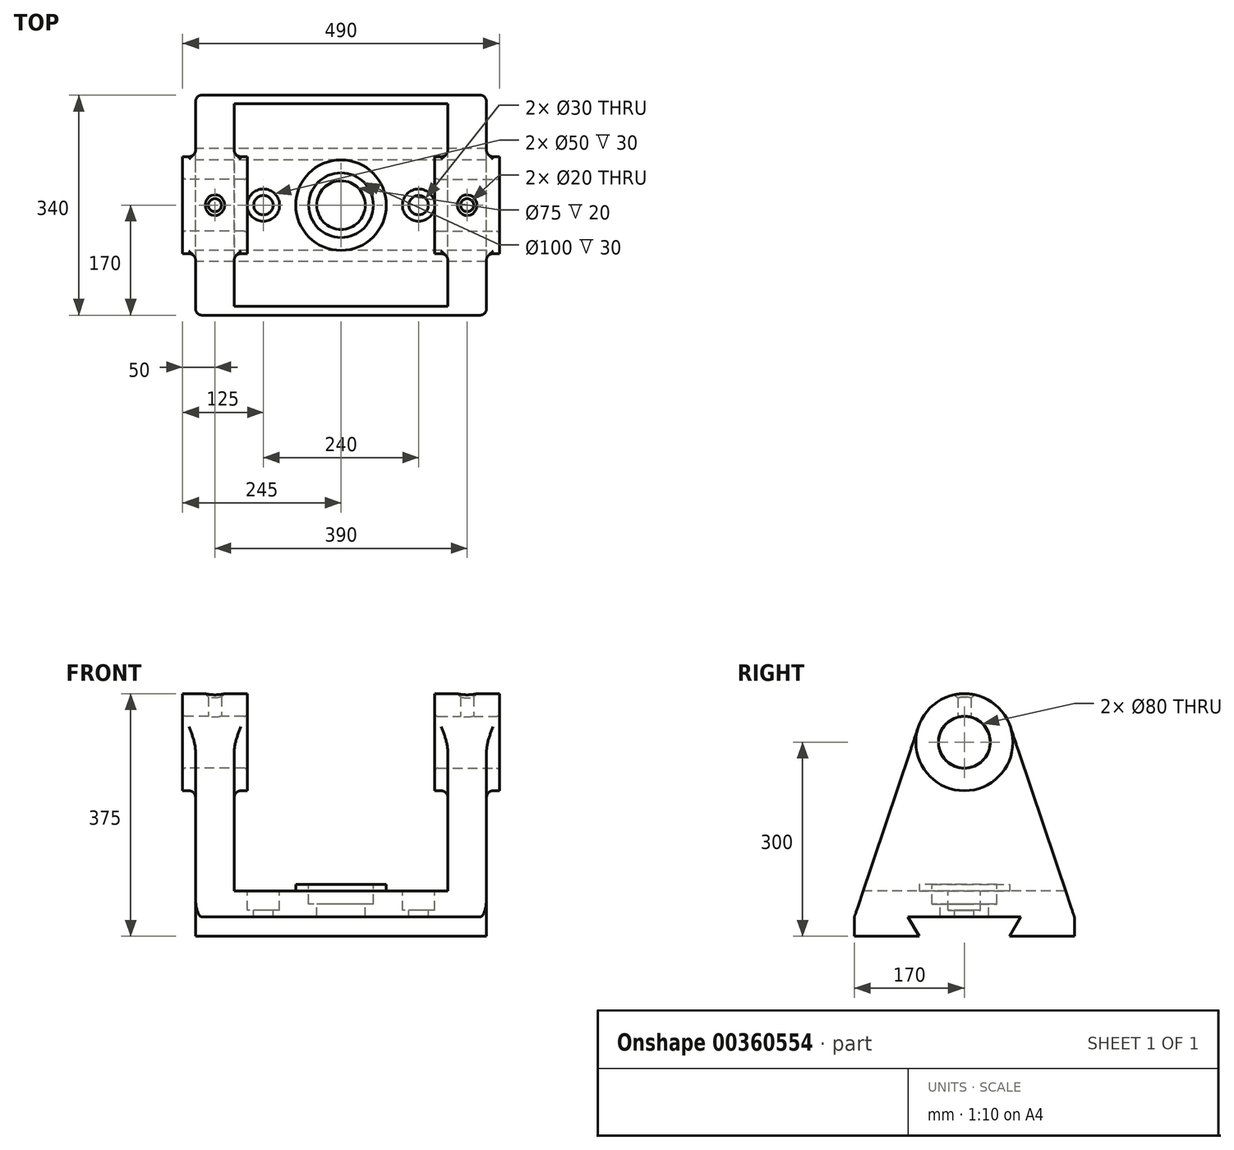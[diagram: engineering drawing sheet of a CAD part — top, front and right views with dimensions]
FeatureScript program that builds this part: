
annotation { "Feature Type Name" : "Feature", "Feature Type Description" : "" }
export const myFeature = defineFeature(function(context is Context, id is Id, definition is map)
    precondition{}
    {
        {
            var Q0;
            Q0=qCreatedBy(makeId("Right.planeOp"),FACE);
            var sketch = newSketch(context, id + "F0", { "sketchPlane" : qUnion([Q0])});
            skArc(sketch, "E0", {"start": v(71.08, 23.92) * mm, "mid": v(0, 75) * mm, "end": v(-71.08, 23.92) * mm});
            skLineSegment(sketch, "E1", {"start": v(0, 0) * mm, "end": v(0, -300) * mm, "construction": true});
            skLineSegment(sketch, "E2", {"start": v(0, -300) * mm, "end": v(70, -300) * mm, "construction": true});
            skLineSegment(sketch, "E3", {"start": v(70, -300) * mm, "end": v(170, -300) * mm});
            skLineSegment(sketch, "E4", {"start": v(170, -300) * mm, "end": v(170, -270) * mm});
            skLineSegment(sketch, "E5", {"start": v(170, -270) * mm, "end": v(71.08, 23.92) * mm});
            skLineSegment(sketch, "E6", {"start": v(70, -270) * mm, "end": v(87.32, -270) * mm, "construction": true});
            skLineSegment(sketch, "E7", {"start": v(87.32, -270) * mm, "end": v(0, -270) * mm});
            skLineSegment(sketch, "E8", {"start": v(70, -300) * mm, "end": v(87.32, -270) * mm});
            skLineSegment(sketch, "E9.MirrorCS", {"start": v(-87.32, -270) * mm, "end": v(0, -270) * mm});
            skLineSegment(sketch, "E10.MirrorCS", {"start": v(-70, -300) * mm, "end": v(-87.32, -270) * mm});
            skLineSegment(sketch, "E11.MirrorCS", {"start": v(-70, -300) * mm, "end": v(-170, -300) * mm});
            skLineSegment(sketch, "E12.MirrorCS", {"start": v(-170, -300) * mm, "end": v(-170, -270) * mm});
            skLineSegment(sketch, "E13.MirrorCS", {"start": v(-170, -270) * mm, "end": v(-71.08, 23.92) * mm});
            skSolve(sketch);
        }
        {
            var Q0;
            Q0 = qSketchRegion(id + "F0", true);
            extrude(context, id + "F1", {"entities" : qUnion([Q0]), "depth" : 60 * mm});
        }
        {
            var Q0;
            Q0=makeQuery(id+"F1.opExtrude","CAP_FACE",FACE,{"disambiguationData":[OSD([sQuery(id+"F0.wireOp",EDGE,"E0"),sQuery(id+"F0.wireOp",EDGE,"E3"),sQuery(id+"F0.wireOp",EDGE,"E4"),sQuery(id+"F0.wireOp",EDGE,"E5"),sQuery(id+"F0.wireOp",EDGE,"E7"),sQuery(id+"F0.wireOp",EDGE,"E8"),sQuery(id+"F0.wireOp",EDGE,"E9.MirrorCS"),sQuery(id+"F0.wireOp",EDGE,"E10.MirrorCS"),sQuery(id+"F0.wireOp",EDGE,"E11.MirrorCS"),sQuery(id+"F0.wireOp",EDGE,"E12.MirrorCS"),sQuery(id+"F0.wireOp",EDGE,"E13.MirrorCS")])],"isStart":false});
            var sketch = newSketch(context, id + "F2", { "sketchPlane" : qUnion([Q0])});
            skCircle(sketch, "E14", {"center": v(0, 0) * mm, "radius": 75 * mm});
            skCircle(sketch, "E15", {"center": v(0, 0) * mm, "radius": 40 * mm});
            skSolve(sketch);
        }
        {
            var Q0;
            Q0 = qSketchRegion(id + "F2", true);
            extrude(context, id + "F3", {"entities" : qUnion([Q0]), "operationType" : NewBodyOperationType.ADD, "depth" : 20 * mm, "hasSecondDirection" : true, "secondDirectionOppositeDirection" : true, "secondDirectionDepth" : 80 * mm});
        }
        {
            var Q0;
            Q0=makeQuery(id+"F3.boolean.opBoolean","SPLIT",FACE,{"disambiguationData":[TD([makeQuery(id+"F3.opExtrude","SWEPT_FACE",FACE,{"disambiguationData":[OSD([sQuery(id+"F2.wireOp",EDGE,"E15")])]})])],"derivedFrom":makeQuery(id+"F1.opExtrude","CAP_FACE",FACE,{"disambiguationData":[OSD([sQuery(id+"F0.wireOp",EDGE,"E0"),sQuery(id+"F0.wireOp",EDGE,"E3"),sQuery(id+"F0.wireOp",EDGE,"E4"),sQuery(id+"F0.wireOp",EDGE,"E5"),sQuery(id+"F0.wireOp",EDGE,"E7"),sQuery(id+"F0.wireOp",EDGE,"E8"),sQuery(id+"F0.wireOp",EDGE,"E9.MirrorCS"),sQuery(id+"F0.wireOp",EDGE,"E10.MirrorCS"),sQuery(id+"F0.wireOp",EDGE,"E11.MirrorCS"),sQuery(id+"F0.wireOp",EDGE,"E12.MirrorCS"),sQuery(id+"F0.wireOp",EDGE,"E13.MirrorCS")])],"isStart":true})});
            extrude(context, id + "F4", {"entities" : qUnion([Q0]), "operationType" : NewBodyOperationType.REMOVE, "endBound" : BoundingType.THROUGH_ALL, "oppositeDirection" : true, "depth" : 25 * mm});
        }
        {
            var Q0;
            Q0=makeQuery(id+"F3.boolean.opBoolean","INTERSECT",EDGE,{"derivedFrom":[makeQuery(id+"F1.opExtrude","CAP_FACE",FACE,{"disambiguationData":[OSD([sQuery(id+"F0.wireOp",EDGE,"E0"),sQuery(id+"F0.wireOp",EDGE,"E3"),sQuery(id+"F0.wireOp",EDGE,"E4"),sQuery(id+"F0.wireOp",EDGE,"E5"),sQuery(id+"F0.wireOp",EDGE,"E7"),sQuery(id+"F0.wireOp",EDGE,"E8"),sQuery(id+"F0.wireOp",EDGE,"E9.MirrorCS"),sQuery(id+"F0.wireOp",EDGE,"E10.MirrorCS"),sQuery(id+"F0.wireOp",EDGE,"E11.MirrorCS"),sQuery(id+"F0.wireOp",EDGE,"E12.MirrorCS"),sQuery(id+"F0.wireOp",EDGE,"E13.MirrorCS")])],"isStart":true}),makeQuery(id+"F3.opExtrude","SWEPT_FACE",FACE,{"disambiguationData":[OSD([sQuery(id+"F2.wireOp",EDGE,"E14")])]})]});
            var Q1;
            Q1=makeQuery(id+"F3.boolean.opBoolean","INTERSECT",EDGE,{"derivedFrom":[makeQuery(id+"F1.opExtrude","CAP_FACE",FACE,{"disambiguationData":[OSD([sQuery(id+"F0.wireOp",EDGE,"E0"),sQuery(id+"F0.wireOp",EDGE,"E3"),sQuery(id+"F0.wireOp",EDGE,"E4"),sQuery(id+"F0.wireOp",EDGE,"E5"),sQuery(id+"F0.wireOp",EDGE,"E7"),sQuery(id+"F0.wireOp",EDGE,"E8"),sQuery(id+"F0.wireOp",EDGE,"E9.MirrorCS"),sQuery(id+"F0.wireOp",EDGE,"E10.MirrorCS"),sQuery(id+"F0.wireOp",EDGE,"E11.MirrorCS"),sQuery(id+"F0.wireOp",EDGE,"E12.MirrorCS"),sQuery(id+"F0.wireOp",EDGE,"E13.MirrorCS")])],"isStart":false}),makeQuery(id+"F3.opExtrude","SWEPT_FACE",FACE,{"disambiguationData":[OSD([sQuery(id+"F2.wireOp",EDGE,"E14")])]})]});
            fillet(context, id + "F5", {"entities" : qUnion([Q0, Q1]), "radius" : 10 * mm, "tangentPropagation" : true, "allowEdgeOverflow" : false});
        }
        {
            var Q0;
            Q0=qCreatedBy(makeId("Right.planeOp"),FACE);
            cPlane(context, id + "F6", {"entities" : qUnion([Q0]), "cplaneType" : CPlaneType.OFFSET, "offset" : 225 * mm, "width" : 150 * mm, "height" : 150 * mm});
        }
        {
            var Q0;
            Q0=qCreatedBy(id+"F6.planeOp",FACE);
            var sketch = newSketch(context, id + "F7", { "sketchPlane" : qUnion([Q0])});
            skLineSegment(sketch, "E16.0", {"start": v(0, 0) * mm, "end": v(0, -300) * mm});
            skSolve(sketch);
        }
        {
            var Q0;
            Q0=makeQuery(id+"F1.opExtrude","SWEPT_BODY",BODY,{"disambiguationData":[OSD([sQuery(id+"F0.wireOp",EDGE,"E0"),sQuery(id+"F0.wireOp",EDGE,"E3"),sQuery(id+"F0.wireOp",EDGE,"E4"),sQuery(id+"F0.wireOp",EDGE,"E5"),sQuery(id+"F0.wireOp",EDGE,"E7"),sQuery(id+"F0.wireOp",EDGE,"E8"),sQuery(id+"F0.wireOp",EDGE,"E9.MirrorCS"),sQuery(id+"F0.wireOp",EDGE,"E10.MirrorCS"),sQuery(id+"F0.wireOp",EDGE,"E11.MirrorCS"),sQuery(id+"F0.wireOp",EDGE,"E12.MirrorCS"),sQuery(id+"F0.wireOp",EDGE,"E13.MirrorCS")])]});
            var Q1;
            Q1=qCreatedBy(id+"F6.planeOp",FACE);
            mirror(context, id + "F8", {"operationType" : NewBodyOperationType.ADD, "entities" : qUnion([Q0]), "mirrorPlane" : qUnion([Q1])});
        }
        {
            var Q0;
            {var subQ0=sQuery(id+"F0.wireOp",EDGE,"E12.MirrorCS");var subQ1=sQuery(id+"F0.wireOp",EDGE,"E11.MirrorCS");var subQ2=sQuery(id+"F0.wireOp",EDGE,"E10.MirrorCS");var subQ3=sQuery(id+"F0.wireOp",EDGE,"E8");var subQ4=sQuery(id+"F0.wireOp",EDGE,"E9.MirrorCS");var subQ5=sQuery(id+"F0.wireOp",EDGE,"E7");var subQ6=sQuery(id+"F0.wireOp",EDGE,"E13.MirrorCS");var subQ7=sQuery(id+"F0.wireOp",EDGE,"E0");var subQ8=sQuery(id+"F0.wireOp",EDGE,"E5");var subQ9=sQuery(id+"F0.wireOp",EDGE,"E3");var subQ10=sQuery(id+"F0.wireOp",EDGE,"E4");Q0=makeQuery(id+"F8.opPattern","COPY",FACE,{"derivedFrom":makeQuery(id+"F3.boolean.opBoolean","SPLIT",FACE,{"disambiguationData":[TD([makeQuery(id+"F1.opExtrude","SWEPT_FACE",FACE,{"disambiguationData":[OSD([subQ7])]})])],"derivedFrom":makeQuery(id+"F1.opExtrude","CAP_FACE",FACE,{"disambiguationData":[OSD([subQ7,subQ9,subQ10,subQ8,subQ5,subQ3,subQ4,subQ2,subQ1,subQ0,subQ6])],"isStart":false})}),"instanceName":"1"});}
            var sketch = newSketch(context, id + "F9", { "sketchPlane" : qUnion([Q0])});
            skPoint(sketch, "E17.0", {"position": v(170, -285) * mm});
            skPoint(sketch, "E18.0", {"position": v(120, -300) * mm});
            skPoint(sketch, "E19.0", {"position": v(78.66, -285) * mm});
            skLineSegment(sketch, "E20.0", {"start": v(87.32, -270) * mm, "end": v(-87.32, -270) * mm});
            skPoint(sketch, "E21.0", {"position": v(-78.66, -285) * mm});
            skPoint(sketch, "E22.0", {"position": v(-120, -300) * mm});
            skLineSegment(sketch, "E23.0", {"start": v(-170, -300) * mm, "end": v(-170, -270) * mm});
            skLineSegment(sketch, "E24", {"start": v(87.32, -270) * mm, "end": v(87.32, -230) * mm, "construction": true});
            skLineSegment(sketch, "E25", {"start": v(87.32, -230) * mm, "end": v(156.54, -230) * mm, "construction": true});
            skLineSegment(sketch, "E26", {"start": v(156.54, -230) * mm, "end": v(-156.54, -230) * mm});
            skLineSegment(sketch, "E27", {"start": v(170, -270) * mm, "end": v(156.54, -230) * mm});
            skLineSegment(sketch, "E28", {"start": v(-170, -270) * mm, "end": v(-156.54, -230) * mm});
            skLineSegment(sketch, "E29", {"start": v(170, -270) * mm, "end": v(170, -300) * mm});
            skLineSegment(sketch, "E30", {"start": v(170, -300) * mm, "end": v(70, -300) * mm});
            skLineSegment(sketch, "E31", {"start": v(70, -300) * mm, "end": v(87.32, -270) * mm});
            skLineSegment(sketch, "E32", {"start": v(-87.32, -270) * mm, "end": v(-70, -300) * mm});
            skLineSegment(sketch, "E33", {"start": v(-70, -300) * mm, "end": v(-170, -300) * mm});
            skSolve(sketch);
        }
        {
            var Q0;
            Q0 = qSketchRegion(id + "F9", true);
            var Q1;
            {var subQ0=sQuery(id+"F0.wireOp",EDGE,"E12.MirrorCS");var subQ1=sQuery(id+"F0.wireOp",EDGE,"E11.MirrorCS");var subQ2=sQuery(id+"F0.wireOp",EDGE,"E10.MirrorCS");var subQ3=sQuery(id+"F0.wireOp",EDGE,"E8");var subQ4=sQuery(id+"F0.wireOp",EDGE,"E9.MirrorCS");var subQ5=sQuery(id+"F0.wireOp",EDGE,"E7");var subQ6=sQuery(id+"F0.wireOp",EDGE,"E13.MirrorCS");var subQ7=sQuery(id+"F0.wireOp",EDGE,"E0");var subQ8=sQuery(id+"F0.wireOp",EDGE,"E5");var subQ9=sQuery(id+"F0.wireOp",EDGE,"E3");var subQ10=sQuery(id+"F0.wireOp",EDGE,"E4");Q1=makeQuery(id+"F3.boolean.opBoolean","SPLIT",FACE,{"disambiguationData":[TD([makeQuery(id+"F1.opExtrude","SWEPT_FACE",FACE,{"disambiguationData":[OSD([subQ7])]})])],"derivedFrom":makeQuery(id+"F1.opExtrude","CAP_FACE",FACE,{"disambiguationData":[OSD([subQ7,subQ9,subQ10,subQ8,subQ5,subQ3,subQ4,subQ2,subQ1,subQ0,subQ6])],"isStart":false})});}
            extrude(context, id + "F10", {"entities" : qUnion([Q0]), "operationType" : NewBodyOperationType.ADD, "endBound" : BoundingType.UP_TO_SURFACE, "endBoundEntityFace" : qUnion([Q1]), "depth" : 25 * mm});
        }
        {
            var Q0;
            Q0=makeQuery(id+"F10.opExtrude","SWEPT_FACE",FACE,{"disambiguationData":[OSD([sQuery(id+"F9.wireOp",EDGE,"E26")])]});
            var sketch = newSketch(context, id + "F11", { "sketchPlane" : qUnion([Q0])});
            skPoint(sketch, "E34.0", {"position": v(225, 0) * mm});
            skCircle(sketch, "E35", {"center": v(225, 0) * mm, "radius": 70 * mm});
            skLineSegment(sketch, "E36", {"start": v(60, 156.54) * mm, "end": v(225, 156.54) * mm, "construction": true});
            skSolve(sketch);
        }
        {
            var Q0;
            Q0 = qSketchRegion(id + "F11", true);
            extrude(context, id + "F12", {"entities" : qUnion([Q0]), "operationType" : NewBodyOperationType.ADD, "depth" : 10 * mm});
        }
        {
            var Q0;
            Q0=makeQuery(id+"F12.opExtrude","CAP_EDGE",EDGE,{"disambiguationData":[OSD([sQuery(id+"F11.wireOp",EDGE,"E35")])],"isStart":true});
            var Q1;
            Q1=makeQuery(id+"F8.opPattern","COPY",EDGE,{"derivedFrom":makeQuery(id+"F1.opExtrude","CAP_EDGE",EDGE,{"disambiguationData":[OSD([sQuery(id+"F0.wireOp",EDGE,"E12.MirrorCS")])],"isStart":true}),"instanceName":"1"});
            var Q2;
            Q2=makeQuery(id+"F1.opExtrude","CAP_EDGE",EDGE,{"disambiguationData":[OSD([sQuery(id+"F0.wireOp",EDGE,"E12.MirrorCS")])],"isStart":true});
            var Q3;
            Q3=makeQuery(id+"F1.opExtrude","CAP_EDGE",EDGE,{"disambiguationData":[OSD([sQuery(id+"F0.wireOp",EDGE,"E4")])],"isStart":true});
            var Q4;
            Q4=makeQuery(id+"F8.opPattern","COPY",EDGE,{"derivedFrom":makeQuery(id+"F1.opExtrude","CAP_EDGE",EDGE,{"disambiguationData":[OSD([sQuery(id+"F0.wireOp",EDGE,"E4")])],"isStart":true}),"instanceName":"1"});
            var Q5;
            Q5=makeQuery(id+"F10.opExtrude","CAP_EDGE",EDGE,{"disambiguationData":[OSD([sQuery(id+"F9.wireOp",EDGE,"E26")])],"isStart":true});
            var Q6;
            Q6=makeQuery(id+"F10.opExtrude","CAP_EDGE",EDGE,{"disambiguationData":[OSD([sQuery(id+"F9.wireOp",EDGE,"E26")])],"isStart":false});
            fillet(context, id + "F13", {"entities" : qUnion([Q0, Q1, Q2, Q3, Q4, Q5, Q6]), "radius" : 10 * mm, "tangentPropagation" : true, "allowEdgeOverflow" : false});
        }
        {
            var Q0;
            Q0=makeQuery(id+"F12.opExtrude","CAP_FACE",FACE,{"disambiguationData":[OSD([sQuery(id+"F11.wireOp",EDGE,"E35")])],"isStart":false});
            var sketch = newSketch(context, id + "F14", { "sketchPlane" : qUnion([Q0])});
            skPoint(sketch, "E37.0", {"position": v(225, 0) * mm});
            skLineSegment(sketch, "E38", {"start": v(225, 0) * mm, "end": v(105, 0) * mm, "construction": true});
            skLineSegment(sketch, "E39", {"start": v(225, 0) * mm, "end": v(345, 0) * mm, "construction": true});
            skSolve(sketch);
        }
        {
            var Q0;
            Q0=sQuery(id+"F14.wireOp",VERTEX,"E37.0");
            var Q1;
            Q1=makeQuery(id+"F1.opExtrude","SWEPT_BODY",BODY,{"disambiguationData":[OSD([sQuery(id+"F0.wireOp",EDGE,"E0"),sQuery(id+"F0.wireOp",EDGE,"E3"),sQuery(id+"F0.wireOp",EDGE,"E4"),sQuery(id+"F0.wireOp",EDGE,"E5"),sQuery(id+"F0.wireOp",EDGE,"E7"),sQuery(id+"F0.wireOp",EDGE,"E8"),sQuery(id+"F0.wireOp",EDGE,"E9.MirrorCS"),sQuery(id+"F0.wireOp",EDGE,"E10.MirrorCS"),sQuery(id+"F0.wireOp",EDGE,"E11.MirrorCS"),sQuery(id+"F0.wireOp",EDGE,"E12.MirrorCS"),sQuery(id+"F0.wireOp",EDGE,"E13.MirrorCS")])]});
            hole(context, id + "F15", {"style" : HoleStyle.C_BORE, "endStyle" : HoleEndStyle.THROUGH, "holeDiameter" : 75 * mm, "cBoreDiameter" : 100 * mm, "cBoreDepth" : 30 * mm, "isTappedThrough" : true, "tappedDepth" : 12 * mm, "tapClearance" : 3, "startFromSketch" : true, "locations" : qUnion([Q0]), "scope" : qUnion([Q1])});
        }
        {
            var Q0;
            Q0=sQuery(id+"F14.wireOp",VERTEX,"E38.end");
            var Q1;
            Q1=sQuery(id+"F14.wireOp",VERTEX,"pOcY5BRp-zrCL-d1PC-rWaC-ocyYlrgYzo9T.end");
            var Q2;
            Q2=sQuery(id+"F14.wireOp",VERTEX,"E39.end");
            var Q3;
            Q3=makeQuery(id+"F1.opExtrude","SWEPT_BODY",BODY,{"disambiguationData":[OSD([sQuery(id+"F0.wireOp",EDGE,"E0"),sQuery(id+"F0.wireOp",EDGE,"E3"),sQuery(id+"F0.wireOp",EDGE,"E4"),sQuery(id+"F0.wireOp",EDGE,"E5"),sQuery(id+"F0.wireOp",EDGE,"E7"),sQuery(id+"F0.wireOp",EDGE,"E8"),sQuery(id+"F0.wireOp",EDGE,"E9.MirrorCS"),sQuery(id+"F0.wireOp",EDGE,"E10.MirrorCS"),sQuery(id+"F0.wireOp",EDGE,"E11.MirrorCS"),sQuery(id+"F0.wireOp",EDGE,"E12.MirrorCS"),sQuery(id+"F0.wireOp",EDGE,"E13.MirrorCS")])]});
            hole(context, id + "F16", {"style" : HoleStyle.C_BORE, "endStyle" : HoleEndStyle.THROUGH, "holeDiameter" : 30 * mm, "cBoreDiameter" : 50 * mm, "cBoreDepth" : 40 * mm, "isTappedThrough" : true, "tappedDepth" : 12 * mm, "tapClearance" : 3, "startFromSketch" : true, "locations" : qUnion([Q0, Q1, Q2]), "scope" : qUnion([Q3])});
        }
        {
            var Q0;
            {var subQ0=makeQuery(id+"F1.opExtrude","SWEPT_FACE",FACE,{"disambiguationData":[OSD([sQuery(id+"F0.wireOp",EDGE,"E11.MirrorCS")])]});Q0=makeQuery(id+"F10.boolean.opBoolean","MERGE",FACE,{"derivedFrom":[subQ0,makeQuery(id+"F8.opPattern","COPY",FACE,{"derivedFrom":subQ0,"instanceName":"1"}),makeQuery(id+"F10.opExtrude","SWEPT_FACE",FACE,{"disambiguationData":[OSD([sQuery(id+"F9.wireOp",EDGE,"E30")])]})]});}
            cPlane(context, id + "F17", {"entities" : qUnion([Q0]), "cplaneType" : CPlaneType.OFFSET, "offset" : 300 * mm, "oppositeDirection" : true, "width" : 150 * mm, "height" : 150 * mm});
        }
        {
            var Q0;
            Q0=qCreatedBy(id+"F17.planeOp",FACE);
            var sketch = newSketch(context, id + "F18", { "sketchPlane" : qUnion([Q0])});
            skPoint(sketch, "E40.0", {"position": v(0, 0) * mm});
            skLineSegment(sketch, "E41", {"start": v(0, 0) * mm, "end": v(30, 0) * mm, "construction": true});
            skCircle(sketch, "E42", {"center": v(30, 0) * mm, "radius": 10 * mm});
            skCircle(sketch, "E43.MirrorC", {"center": v(420, 0) * mm, "radius": 10 * mm});
            skSolve(sketch);
        }
        {
            var Q0;
            Q0 = qSketchRegion(id + "F18", true);
            extrude(context, id + "F19", {"entities" : qUnion([Q0]), "operationType" : NewBodyOperationType.REMOVE, "endBound" : BoundingType.THROUGH_ALL, "oppositeDirection" : true, "depth" : 25 * mm});
        }
        {
            var Q0;
            Q0=makeQuery(id+"F16.hole-1.boolean.opBoolean","INTERSECT",EDGE,{"derivedFrom":[makeQuery(id+"F10.opExtrude","SWEPT_FACE",FACE,{"disambiguationData":[OSD([sQuery(id+"F9.wireOp",EDGE,"E26")])]}),makeQuery(id+"F16.hole-1.opRevolve","SWEPT_FACE",FACE,{"disambiguationData":[OSD([sQuery(id+"F16.hole-1.sketch.wireOp",EDGE,"cbore_start_line_2")])]})]});
            var Q1;
            Q1=makeQuery(id+"F8.opPattern","COPY",EDGE,{"derivedFrom":makeQuery(id+"F3.opExtrude","CAP_EDGE",EDGE,{"disambiguationData":[OSD([sQuery(id+"F2.wireOp",EDGE,"E15")])],"isStart":false}),"instanceName":"1"});
            var Q2;
            Q2=makeQuery(id+"F3.opExtrude","CAP_EDGE",EDGE,{"disambiguationData":[OSD([sQuery(id+"F2.wireOp",EDGE,"E15")])],"isStart":true});
            var Q3;
            Q3=makeQuery(id+"F16.hole-0.boolean.opBoolean","INTERSECT",EDGE,{"derivedFrom":[makeQuery(id+"F10.opExtrude","SWEPT_FACE",FACE,{"disambiguationData":[OSD([sQuery(id+"F9.wireOp",EDGE,"E26")])]}),makeQuery(id+"F16.hole-0.opRevolve","SWEPT_FACE",FACE,{"disambiguationData":[OSD([sQuery(id+"F16.hole-0.sketch.wireOp",EDGE,"cbore_start_line_2")])]})]});
            var Q4;
            Q4=makeQuery(id+"F3.opExtrude","CAP_EDGE",EDGE,{"disambiguationData":[OSD([sQuery(id+"F2.wireOp",EDGE,"E15")])],"isStart":false});
            var Q5;
            Q5=makeQuery(id+"F8.opPattern","COPY",EDGE,{"derivedFrom":makeQuery(id+"F3.opExtrude","CAP_EDGE",EDGE,{"disambiguationData":[OSD([sQuery(id+"F2.wireOp",EDGE,"E15")])],"isStart":true}),"instanceName":"1"});
            fillet(context, id + "F20", {"entities" : qUnion([Q0, Q1, Q2, Q3, Q4, Q5]), "radius" : 5 * mm, "tangentPropagation" : true, "allowEdgeOverflow" : false});
        }
        {
            var Q0;
            Q0=makeQuery(id+"F19.boolean.opBoolean","INTERSECT",EDGE,{"derivedFrom":[makeQuery(id+"F8.opPattern","COPY",FACE,{"derivedFrom":makeQuery(id+"F3.boolean.opBoolean","MERGE",FACE,{"derivedFrom":[makeQuery(id+"F1.opExtrude","SWEPT_FACE",FACE,{"disambiguationData":[OSD([sQuery(id+"F0.wireOp",EDGE,"E0")])]}),makeQuery(id+"F3.opExtrude","SWEPT_FACE",FACE,{"disambiguationData":[OSD([sQuery(id+"F2.wireOp",EDGE,"E14")])]})]}),"instanceName":"1"}),makeQuery(id+"F19.opExtrude","SWEPT_FACE",FACE,{"disambiguationData":[OSD([sQuery(id+"F18.wireOp",EDGE,"E43.MirrorC")])]})]});
            var Q1;
            Q1=makeQuery(id+"F19.boolean.opBoolean","INTERSECT",EDGE,{"derivedFrom":[makeQuery(id+"F3.boolean.opBoolean","MERGE",FACE,{"derivedFrom":[makeQuery(id+"F1.opExtrude","SWEPT_FACE",FACE,{"disambiguationData":[OSD([sQuery(id+"F0.wireOp",EDGE,"E0")])]}),makeQuery(id+"F3.opExtrude","SWEPT_FACE",FACE,{"disambiguationData":[OSD([sQuery(id+"F2.wireOp",EDGE,"E14")])]})]}),makeQuery(id+"F19.opExtrude","SWEPT_FACE",FACE,{"disambiguationData":[OSD([sQuery(id+"F18.wireOp",EDGE,"E42")])]})]});
            chamfer(context, id + "F21", {"entities" : qUnion([Q0, Q1]), "width" : 5 * mm, "tangentPropagation" : true});
        }
    });
